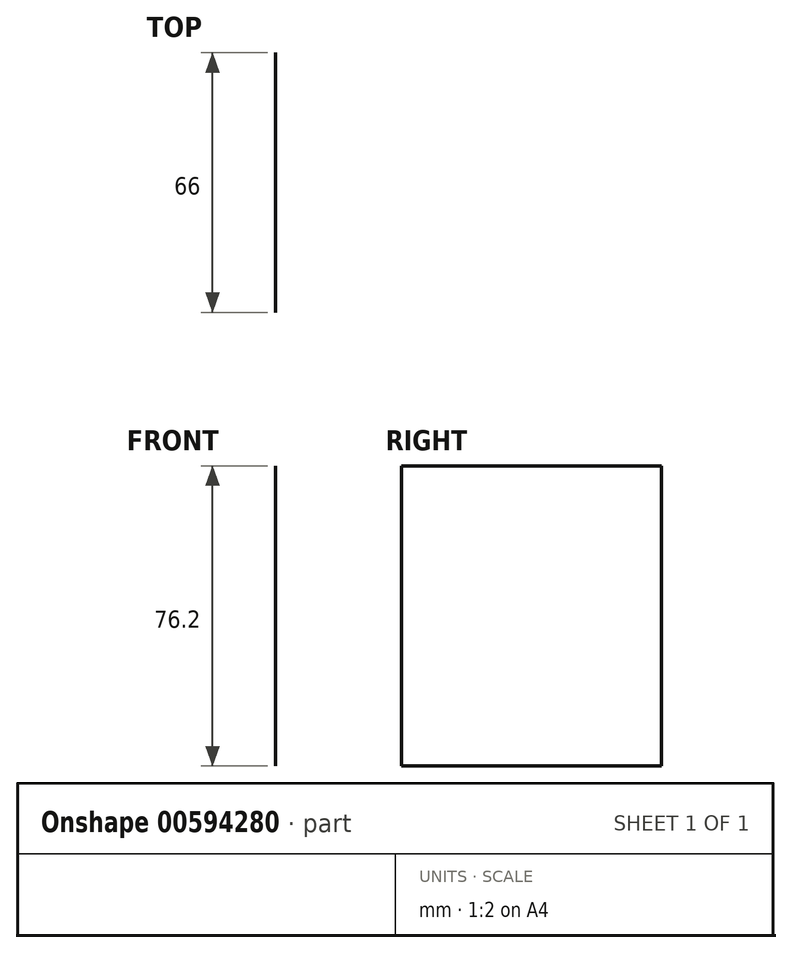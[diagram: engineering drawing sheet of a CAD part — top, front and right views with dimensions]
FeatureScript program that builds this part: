
annotation { "Feature Type Name" : "Feature", "Feature Type Description" : "" }
export const myFeature = defineFeature(function(context is Context, id is Id, definition is map)
    precondition{}
    {
        {
            var Q0;
            Q0=qCreatedBy(makeId("Top.planeOp"),FACE);
            var sketch = newSketch(context, id + "F0", { "sketchPlane" : qUnion([Q0])});
            skLineSegment(sketch, "E0.bottom", {"start": v(-80.06, 62.07) * mm, "end": v(94.56, 62.07) * mm});
            skLineSegment(sketch, "E0.top", {"start": v(-80.06, -3.93) * mm, "end": v(94.56, -3.93) * mm});
            skLineSegment(sketch, "E0.left", {"start": v(-80.06, 62.07) * mm, "end": v(-80.06, -3.93) * mm});
            skLineSegment(sketch, "E0.right", {"start": v(94.56, 62.07) * mm, "end": v(94.56, -3.93) * mm});
            skLineSegment(sketch, "E1.bottom", {"start": v(16.72, 62.07) * mm, "end": v(-79.77, 62.07) * mm, "construction": true});
            skLineSegment(sketch, "E1.top", {"start": v(16.72, -3.93) * mm, "end": v(-79.77, -3.93) * mm, "construction": true});
            skLineSegment(sketch, "E1.left", {"start": v(16.72, 62.07) * mm, "end": v(16.72, -3.93) * mm});
            skLineSegment(sketch, "E1.right", {"start": v(-79.77, 62.07) * mm, "end": v(-79.77, -3.93) * mm});
            skPoint(sketch, "E2.oppositeSnap0", {"position": v(-31.53, 62.07) * mm});
            skLineSegment(sketch, "E2.bottom", {"start": v(-31.53, 62.07) * mm, "end": v(-31.53, 62.07) * mm});
            skLineSegment(sketch, "E2.top", {"start": v(-31.53, 54.03) * mm, "end": v(-31.53, 54.03) * mm});
            skLineSegment(sketch, "E2.left", {"start": v(-31.53, 54.03) * mm, "end": v(-31.53, 62.07) * mm});
            skLineSegment(sketch, "E2.right", {"start": v(-31.53, 54.03) * mm, "end": v(-31.53, 62.07) * mm});
            skSolve(sketch);
        }
        {
            var Q0;
            Q0=sQuery(id+"F0.wireOp",EDGE,"E0.left");
            extrude(context, id + "F1", {"bodyType" : ToolBodyType.SURFACE, "surfaceEntities" : qUnion([Q0]), "endBound" : BoundingType.SYMMETRIC, "depth" : 76.2 * mm, "offsetDistance" : 25.4 * mm});
        }
    });
